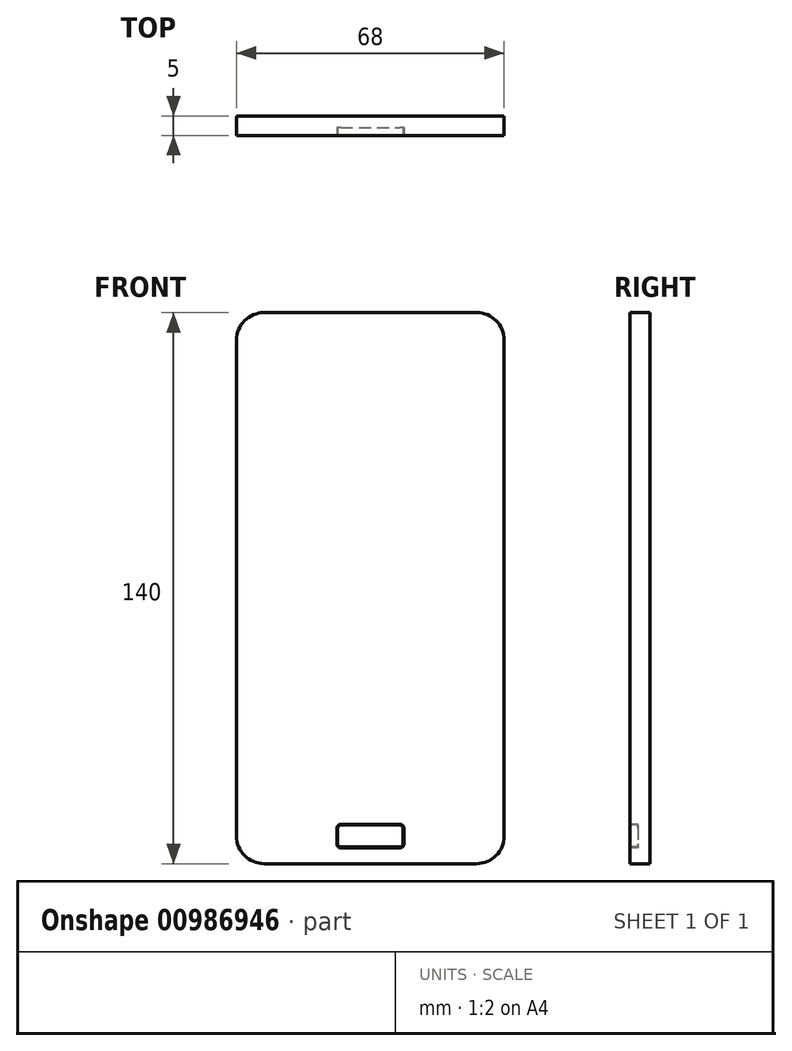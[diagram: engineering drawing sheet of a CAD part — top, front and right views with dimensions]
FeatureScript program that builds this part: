
annotation { "Feature Type Name" : "Feature", "Feature Type Description" : "" }
export const myFeature = defineFeature(function(context is Context, id is Id, definition is map)
    precondition{}
    {
        {
            var Q0;
            Q0=qCreatedBy(makeId("Front.planeOp"),FACE);
            var sketch = newSketch(context, id + "F0", { "sketchPlane" : qUnion([Q0])});
            skLineSegment(sketch, "E0.bottom", {"start": v(-34, 70) * mm, "end": v(34, 70) * mm});
            skLineSegment(sketch, "E0.top", {"start": v(-34, -70) * mm, "end": v(34, -70) * mm});
            skLineSegment(sketch, "E0.left", {"start": v(-34, 70) * mm, "end": v(-34, -70) * mm});
            skLineSegment(sketch, "E0.right", {"start": v(34, 70) * mm, "end": v(34, -70) * mm});
            skPoint(sketch, "E0.middle", {"position": v(0, 0) * mm});
            skSolve(sketch);
        }
        {
            var Q0;
            Q0 = qSketchRegion(id + "F0", true);
            extrude(context, id + "F1", {"entities" : qUnion([Q0]), "endBound" : BoundingType.SYMMETRIC, "depth" : 5 * mm, "offsetDistance" : 25 * mm});
        }
        {
            var Q0;
            Q0=makeQuery(id+"F1.opExtrude","SWEPT_EDGE",EDGE,{"disambiguationData":[OSD([sQuery(id+"F0.wireOp",EDGE,"E0.bottom"),sQuery(id+"F0.wireOp",EDGE,"E0.right")])]});
            var Q1;
            Q1=makeQuery(id+"F1.opExtrude","SWEPT_EDGE",EDGE,{"disambiguationData":[OSD([sQuery(id+"F0.wireOp",EDGE,"E0.bottom"),sQuery(id+"F0.wireOp",EDGE,"E0.left")])]});
            var Q2;
            Q2=makeQuery(id+"F1.opExtrude","SWEPT_EDGE",EDGE,{"disambiguationData":[OSD([sQuery(id+"F0.wireOp",EDGE,"E0.top"),sQuery(id+"F0.wireOp",EDGE,"E0.right")])]});
            var Q3;
            Q3=makeQuery(id+"F1.opExtrude","SWEPT_EDGE",EDGE,{"disambiguationData":[OSD([sQuery(id+"F0.wireOp",EDGE,"E0.top"),sQuery(id+"F0.wireOp",EDGE,"E0.left")])]});
            fillet(context, id + "F2", {"entities" : qUnion([Q0, Q1, Q2, Q3]), "radius" : 7 * mm, "tangentPropagation" : true, "allowEdgeOverflow" : false});
        }
        {
            var Q0;
            Q0=makeQuery(id+"F1.opExtrude","CAP_FACE",FACE,{"disambiguationData":[OSD([sQuery(id+"F0.wireOp",EDGE,"E0.bottom"),sQuery(id+"F0.wireOp",EDGE,"E0.top"),sQuery(id+"F0.wireOp",EDGE,"E0.left"),sQuery(id+"F0.wireOp",EDGE,"E0.right")])],"isStart":false});
            var sketch = newSketch(context, id + "F3", { "sketchPlane" : qUnion([Q0])});
            skLineSegment(sketch, "E1.bottom", {"start": v(-7.5, -60) * mm, "end": v(7.5, -60) * mm});
            skLineSegment(sketch, "E1.top", {"start": v(-7.5, -66) * mm, "end": v(7.5, -66) * mm});
            skLineSegment(sketch, "E1.left", {"start": v(-8.5, -61) * mm, "end": v(-8.5, -65) * mm});
            skLineSegment(sketch, "E1.right", {"start": v(8.5, -61) * mm, "end": v(8.5, -65) * mm});
            skPoint(sketch, "E2.visualSharp", {"position": v(-8.5, -60) * mm});
            skArc(sketch, "E2.filletArc", {"start": v(-7.5, -60) * mm, "mid": v(-8.2, -60.3) * mm, "end": v(-8.5, -61) * mm});
            skPoint(sketch, "E3.visualSharp", {"position": v(8.5, -60) * mm});
            skArc(sketch, "E3.filletArc", {"start": v(8.5, -61) * mm, "mid": v(8.2, -60.3) * mm, "end": v(7.5, -60) * mm});
            skPoint(sketch, "E4.visualSharp", {"position": v(8.5, -66) * mm});
            skArc(sketch, "E4.filletArc", {"start": v(7.5, -66) * mm, "mid": v(8.2, -65.7) * mm, "end": v(8.5, -65) * mm});
            skPoint(sketch, "E5.visualSharp", {"position": v(-8.5, -66) * mm});
            skArc(sketch, "E5.filletArc", {"start": v(-8.5, -65) * mm, "mid": v(-8.2, -65.7) * mm, "end": v(-7.5, -66) * mm});
            skArc(sketch, "E6.0", {"start": v(-7.5, -60.2) * mm, "mid": v(-8.07, -60.43) * mm, "end": v(-8.3, -61) * mm});
            skLineSegment(sketch, "E6.1", {"start": v(-8.3, -61) * mm, "end": v(-8.3, -65) * mm});
            skLineSegment(sketch, "E6.2", {"start": v(-7.5, -60.2) * mm, "end": v(7.5, -60.2) * mm});
            skArc(sketch, "E6.3", {"start": v(-8.3, -65) * mm, "mid": v(-8.07, -65.57) * mm, "end": v(-7.5, -65.8) * mm});
            skArc(sketch, "E6.4", {"start": v(8.3, -61) * mm, "mid": v(8.07, -60.43) * mm, "end": v(7.5, -60.2) * mm});
            skLineSegment(sketch, "E6.5", {"start": v(8.3, -61) * mm, "end": v(8.3, -65) * mm});
            skArc(sketch, "E6.6", {"start": v(7.5, -65.8) * mm, "mid": v(8.07, -65.57) * mm, "end": v(8.3, -65) * mm});
            skLineSegment(sketch, "E6.7", {"start": v(-7.5, -65.8) * mm, "end": v(7.5, -65.8) * mm});
            skSolve(sketch);
        }
        {
            var Q0;
            Q0 = qSketchRegion(id + "F3", true);
            extrude(context, id + "F4", {"entities" : qUnion([Q0]), "operationType" : NewBodyOperationType.REMOVE, "oppositeDirection" : true, "depth" : 2 * mm, "offsetDistance" : 25 * mm});
        }
    });
